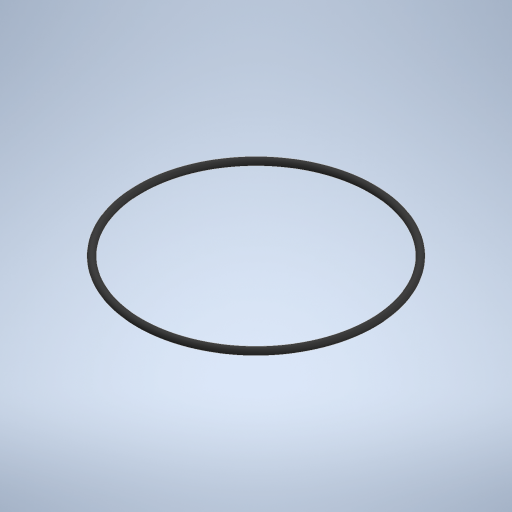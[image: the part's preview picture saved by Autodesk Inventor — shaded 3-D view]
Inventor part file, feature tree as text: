
AUTODESK INVENTOR PART (.ipt)
format: ipt  version: 2024.3 (Build 283343000, 343)  size: 259,584 bytes
history: native  units: mm
features: other x1, revolve x1, sketch x1
ambient origin geometry x8: Origin, YZ Plane, XZ Plane, XY Plane, X Axis, Y Axis, Z Axis, Center Point
bodies: Body1 (feature_tree)
feature tree (3):
  other  "Sólido1"
  revolve  "Revolución1"  Angle=360.0deg
  sketch  "Boceto1"  dims[d0=2.62mm d2=360.0deg d3=44.285mm]
